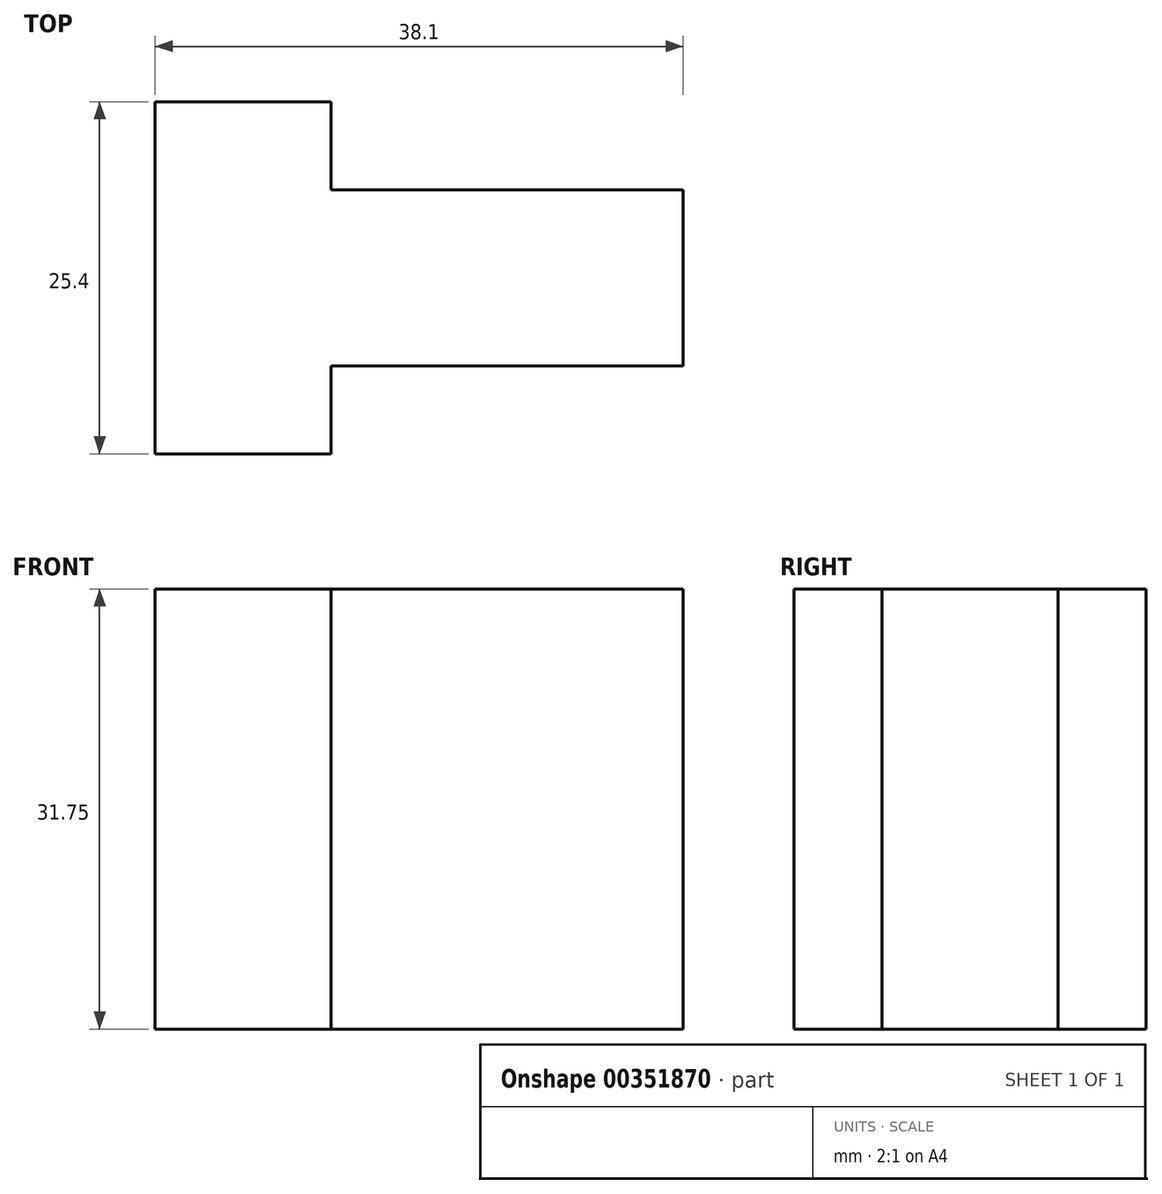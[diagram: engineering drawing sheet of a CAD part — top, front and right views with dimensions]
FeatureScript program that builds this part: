
annotation { "Feature Type Name" : "Feature", "Feature Type Description" : "" }
export const myFeature = defineFeature(function(context is Context, id is Id, definition is map)
    precondition{}
    {
        {
            var Q0;
            Q0=qCreatedBy(makeId("Top.planeOp"),FACE);
            var sketch = newSketch(context, id + "F0", { "sketchPlane" : qUnion([Q0])});
            skLineSegment(sketch, "E0", {"start": v(0, 0) * mm, "end": v(12.7, 0) * mm});
            skLineSegment(sketch, "E1", {"start": v(12.7, 0) * mm, "end": v(12.7, 6.35) * mm});
            skLineSegment(sketch, "E2", {"start": v(12.7, 6.35) * mm, "end": v(38.1, 6.35) * mm});
            skLineSegment(sketch, "E3", {"start": v(38.1, 6.35) * mm, "end": v(38.1, 19.05) * mm});
            skLineSegment(sketch, "E4", {"start": v(12.7, 25.4) * mm, "end": v(0, 25.4) * mm});
            skLineSegment(sketch, "E5", {"start": v(0, 25.4) * mm, "end": v(0, 0) * mm});
            skLineSegment(sketch, "E6", {"start": v(12.7, 25.4) * mm, "end": v(12.7, 19.05) * mm});
            skLineSegment(sketch, "E7", {"start": v(12.7, 19.05) * mm, "end": v(38.1, 19.05) * mm});
            skSolve(sketch);
        }
        {
            var Q0;
            Q0=makeQuery(id+"F0.imprint","IMPRINT",FACE,{"disambiguationData":[TD([[makeQuery(id+"F0.imprint","IMPRINT",EDGE,{"derivedFrom":sQuery(id+"F0.wireOp",EDGE,"E0")}),1.0]])]});
            extrude(context, id + "F1", {"entities" : qUnion([Q0]), "depth" : 31.75 * mm});
        }
    });
